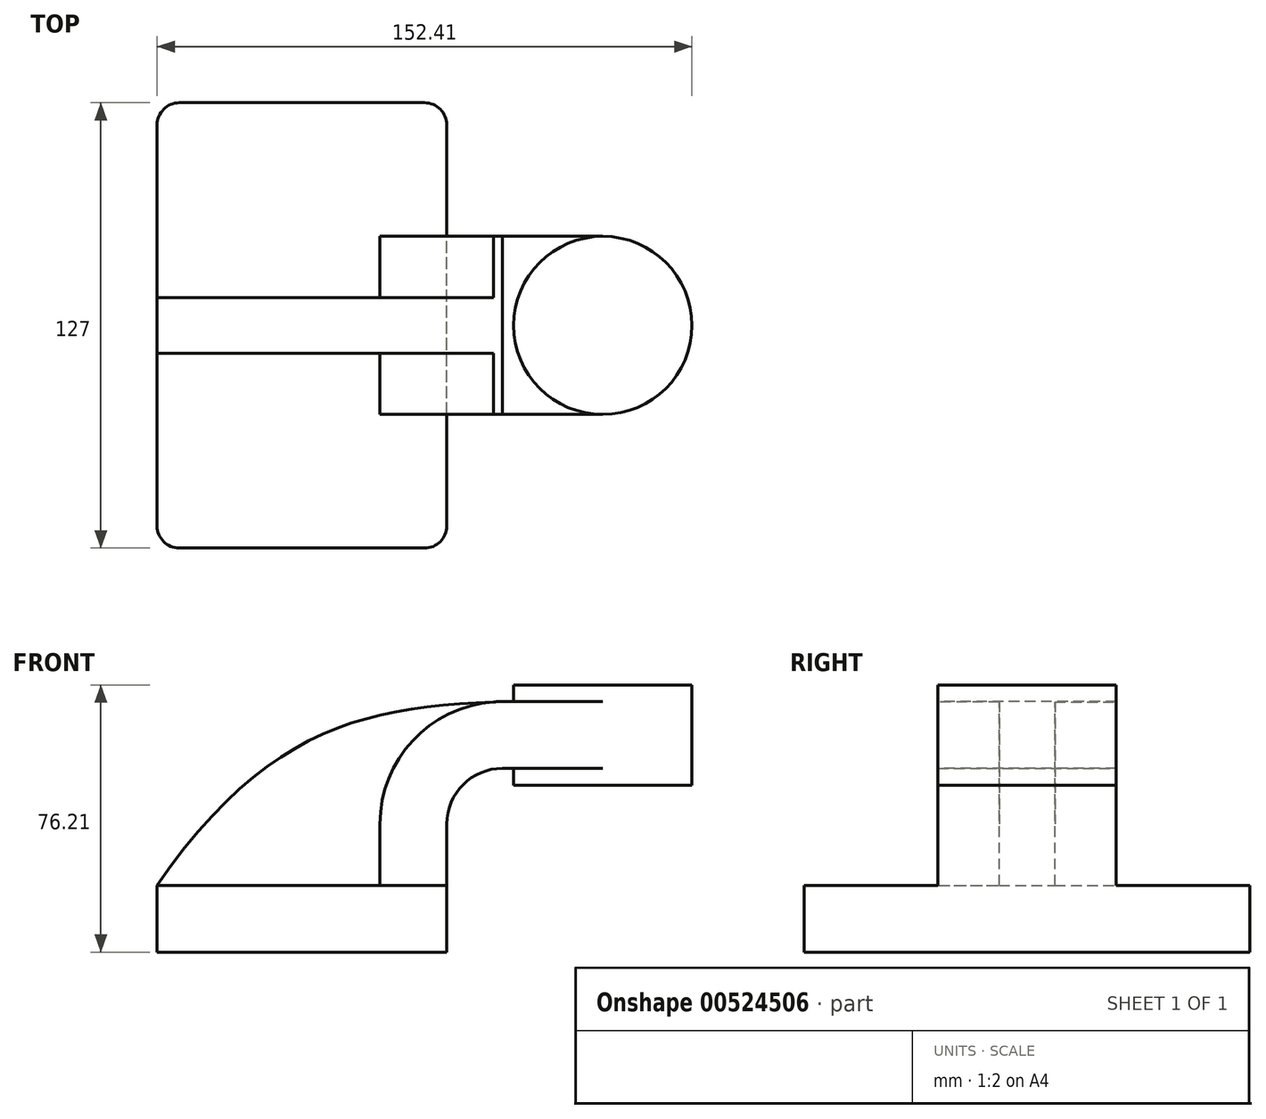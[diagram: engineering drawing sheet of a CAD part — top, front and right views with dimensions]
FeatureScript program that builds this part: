
annotation { "Feature Type Name" : "Feature", "Feature Type Description" : "" }
export const myFeature = defineFeature(function(context is Context, id is Id, definition is map)
    precondition{}
    {
        {
            var Q0;
            Q0=qCreatedBy(makeId("Front.planeOp"),FACE);
            var sketch = newSketch(context, id + "F0", { "sketchPlane" : qUnion([Q0])});
            skLineSegment(sketch, "E0.bottom", {"start": v(-41.28, 9.52) * mm, "end": v(41.28, 9.53) * mm});
            skLineSegment(sketch, "E0.top", {"start": v(-41.28, -9.53) * mm, "end": v(41.28, -9.53) * mm});
            skLineSegment(sketch, "E0.left", {"start": v(-41.28, 9.52) * mm, "end": v(-41.28, -9.53) * mm});
            skLineSegment(sketch, "E0.right", {"start": v(41.28, 9.53) * mm, "end": v(41.28, -9.52) * mm});
            skPoint(sketch, "E0.middle", {"position": v(0, 0) * mm});
            skLineSegment(sketch, "E1.bottom", {"start": v(111.13, 66.67) * mm, "end": v(60.33, 66.67) * mm});
            skLineSegment(sketch, "E1.top", {"start": v(111.13, 38.1) * mm, "end": v(60.33, 38.1) * mm});
            skLineSegment(sketch, "E1.left", {"start": v(111.13, 66.68) * mm, "end": v(111.13, 38.1) * mm});
            skLineSegment(sketch, "E1.right", {"start": v(60.33, 66.68) * mm, "end": v(60.33, 38.1) * mm});
            skPoint(sketch, "E1.middle", {"position": v(85.73, 52.39) * mm});
            skLineSegment(sketch, "E2", {"start": v(41.27, 9.53) * mm, "end": v(41.27, 27) * mm});
            skArc(sketch, "E3", {"start": v(41.27, 27) * mm, "mid": v(45.92, 38.23) * mm, "end": v(57.15, 42.88) * mm});
            skLineSegment(sketch, "E4", {"start": v(57.15, 42.88) * mm, "end": v(85.73, 42.88) * mm});
            skLineSegment(sketch, "E5.0", {"start": v(57.15, 61.93) * mm, "end": v(85.73, 61.93) * mm});
            skArc(sketch, "E5.1", {"start": v(22.22, 27) * mm, "mid": v(32.45, 51.7) * mm, "end": v(57.15, 61.93) * mm});
            skLineSegment(sketch, "E5.2", {"start": v(22.23, 9.53) * mm, "end": v(22.23, 27) * mm});
            skFitSpline(sketch, "E6", {"points": [v(-41.28, 9.52) * mm, v(57.15, 61.93) * mm], "startDerivative": vector(93.6, 135.66) * mm, "endDerivative": vector(117.38, 4.04) * mm});
            skLineSegment(sketch, "E7", {"start": v(85.73, 66.67) * mm, "end": v(85.73, 38.1) * mm});
            skSolve(sketch);
        }
        {
            var Q0;
            Q0=makeQuery(id+"F0.imprint","IMPRINT",FACE,{"disambiguationData":[TD([[makeQuery(id+"F0.imprint","IMPRINT",EDGE,{"derivedFrom":sQuery(id+"F0.wireOp",EDGE,"E0.top")}),1.0]])]});
            extrude(context, id + "F1", {"entities" : qUnion([Q0]), "endBound" : BoundingType.SYMMETRIC, "depth" : 127 * mm, "offsetDistance" : 25.4 * mm});
        }
        {
            var Q0;
            {var subQ1=sQuery(id+"F0.wireOp",EDGE,"E2");Q0=makeQuery(id+"F0.imprint","IMPRINT",FACE,{"disambiguationData":[TD([[makeQuery(id+"F0.imprint","IMPRINT",EDGE,{"derivedFrom":subQ1}),1.0]])]});}
            var Q1;
            {var subQ5=sQuery(id+"F0.wireOp",EDGE,"LwT0piok-D8i5-irN5-Jriw-n6Tzoq0Sis2w");Q1=makeQuery(id+"F0.imprint","IMPRINT",FACE,{"disambiguationData":[TD([[makeQuery(id+"F0.imprint","IMPRINT",EDGE,{"derivedFrom":subQ5}),-1.0]])]});}
            var Q2;
            {var subQ0=sQuery(id+"F0.wireOp",EDGE,"E5.0");var subQ1=sQuery(id+"F0.wireOp",EDGE,"E1.right");var subQ2=makeQuery(id+"F0.imprint","INTERSECT",VERTEX,{"derivedFrom":[subQ1,subQ0]});Q2=makeQuery(id+"F0.imprint","IMPRINT",FACE,{"disambiguationData":[TD([[makeQuery(id+"F0.imprint","IMPRINT",EDGE,{"disambiguationData":[TD([[subQ2,-1.0]])],"derivedFrom":subQ1}),1.0]])]});}
            extrude(context, id + "F2", {"entities" : qUnion([Q0, Q1, Q2]), "operationType" : NewBodyOperationType.ADD, "endBound" : BoundingType.SYMMETRIC, "depth" : 50.8 * mm, "offsetDistance" : 25.4 * mm});
        }
        {
            var Q0;
            {var subQ3=sQuery(id+"F0.wireOp",EDGE,"E5.2");Q0=makeQuery(id+"F0.imprint","IMPRINT",FACE,{"disambiguationData":[TD([[makeQuery(id+"F0.imprint","IMPRINT",EDGE,{"derivedFrom":subQ3}),1.0]])]});}
            extrude(context, id + "F3", {"entities" : qUnion([Q0]), "operationType" : NewBodyOperationType.ADD, "endBound" : BoundingType.SYMMETRIC, "depth" : 15.88 * mm, "offsetDistance" : 25.4 * mm});
        }
        {
            var Q0;
            {var subQ4=sQuery(id+"F0.wireOp",EDGE,"E1.left");Q0=makeQuery(id+"F0.imprint","IMPRINT",FACE,{"disambiguationData":[TD([[makeQuery(id+"F0.imprint","IMPRINT",EDGE,{"derivedFrom":subQ4}),-1.0]])]});}
            var Q1;
            Q1=sQuery(id+"F0.wireOp",EDGE,"E7");
            revolve(context, id + "F4", {"operationType" : NewBodyOperationType.ADD, "entities" : qUnion([Q0]), "axis" : qUnion([Q1]), "revolveType" : RevolveType.FULL});
        }
        {
            var Q0;
            Q0=makeQuery(id+"F1.opExtrude","CAP_EDGE",EDGE,{"disambiguationData":[OSD([sQuery(id+"F0.wireOp",EDGE,"E0.right")])],"isStart":false});
            fillet(context, id + "F5", {"entities" : qUnion([Q0]), "radius" : 6.35 * mm, "tangentPropagation" : true, "allowEdgeOverflow" : false});
        }
        {
            var Q0;
            Q0=makeQuery(id+"F1.opExtrude","CAP_EDGE",EDGE,{"disambiguationData":[OSD([sQuery(id+"F0.wireOp",EDGE,"E0.left")])],"isStart":false});
            fillet(context, id + "F6", {"entities" : qUnion([Q0]), "radius" : 6.35 * mm, "tangentPropagation" : true, "allowEdgeOverflow" : false});
        }
        {
            var Q0;
            Q0=makeQuery(id+"F1.opExtrude","CAP_EDGE",EDGE,{"disambiguationData":[OSD([sQuery(id+"F0.wireOp",EDGE,"E0.left")])],"isStart":true});
            fillet(context, id + "F7", {"entities" : qUnion([Q0]), "radius" : 6.35 * mm, "tangentPropagation" : true, "allowEdgeOverflow" : false});
        }
        {
            var Q0;
            Q0=makeQuery(id+"F1.opExtrude","CAP_EDGE",EDGE,{"disambiguationData":[OSD([sQuery(id+"F0.wireOp",EDGE,"E0.right")])],"isStart":true});
            fillet(context, id + "F8", {"entities" : qUnion([Q0]), "radius" : 6.35 * mm, "tangentPropagation" : true, "allowEdgeOverflow" : false});
        }
    });
